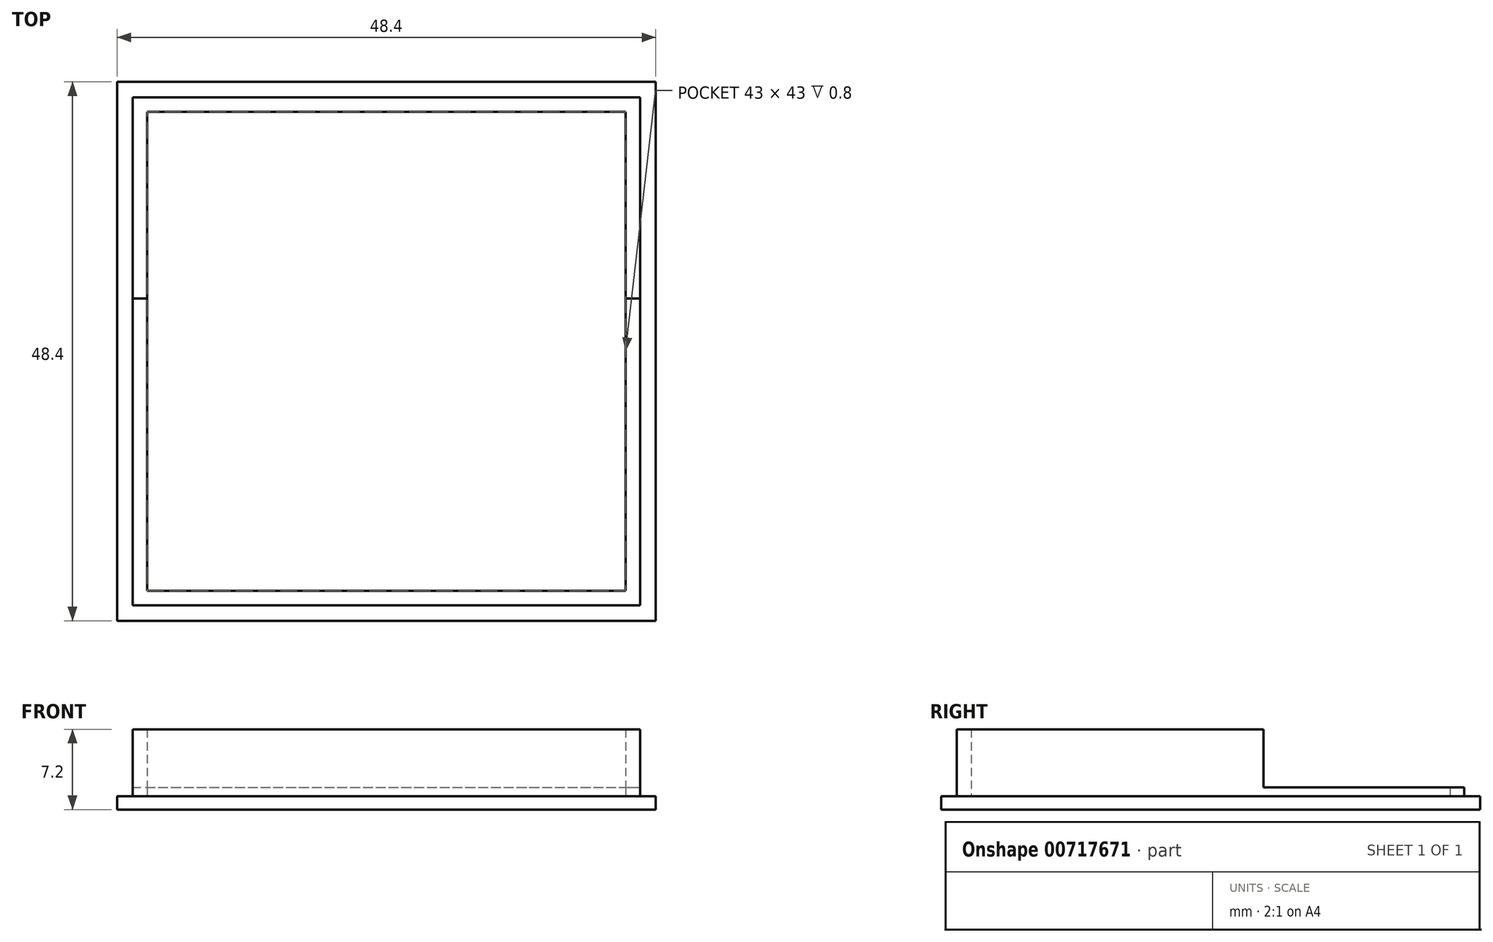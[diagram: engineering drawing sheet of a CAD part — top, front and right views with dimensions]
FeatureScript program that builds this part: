
annotation { "Feature Type Name" : "Feature", "Feature Type Description" : "" }
export const myFeature = defineFeature(function(context is Context, id is Id, definition is map)
    precondition{}
    {
        {
            var Q0;
            Q0=qCreatedBy(makeId("Top.planeOp"),FACE);
            var sketch = newSketch(context, id + "F0", { "sketchPlane" : qUnion([Q0])});
            skLineSegment(sketch, "E0.bottom", {"start": v(-24.2, 23.52) * mm, "end": v(24.2, 23.52) * mm});
            skLineSegment(sketch, "E0.top", {"start": v(-24.2, -24.88) * mm, "end": v(24.2, -24.88) * mm});
            skLineSegment(sketch, "E0.left", {"start": v(-24.2, 23.52) * mm, "end": v(-24.2, -24.88) * mm});
            skLineSegment(sketch, "E0.right", {"start": v(24.2, 23.52) * mm, "end": v(24.2, -24.88) * mm});
            skLineSegment(sketch, "E1.bottom", {"start": v(-22.8, 22.12) * mm, "end": v(22.8, 22.12) * mm});
            skLineSegment(sketch, "E1.top", {"start": v(-22.8, -23.48) * mm, "end": v(22.8, -23.48) * mm});
            skLineSegment(sketch, "E1.left", {"start": v(-22.8, 22.12) * mm, "end": v(-22.8, -23.48) * mm});
            skLineSegment(sketch, "E1.right", {"start": v(22.8, 22.12) * mm, "end": v(22.8, -23.48) * mm});
            skLineSegment(sketch, "E2.bottom", {"start": v(-21.5, 20.82) * mm, "end": v(21.5, 20.82) * mm});
            skLineSegment(sketch, "E2.top", {"start": v(-21.5, -22.18) * mm, "end": v(21.5, -22.18) * mm});
            skLineSegment(sketch, "E2.left", {"start": v(-21.5, 20.82) * mm, "end": v(-21.5, -22.18) * mm});
            skLineSegment(sketch, "E2.right", {"start": v(21.5, 20.82) * mm, "end": v(21.5, -22.18) * mm});
            skLineSegment(sketch, "E3", {"start": v(-22.8, 4.07) * mm, "end": v(-21.5, 4.07) * mm});
            skLineSegment(sketch, "E4", {"start": v(21.5, 4.07) * mm, "end": v(22.8, 4.07) * mm});
            skSolve(sketch);
        }
        {
            var Q0;
            Q0=qCreatedBy(makeId("Top.planeOp"),FACE);
            var sketch = newSketch(context, id + "F1", { "sketchPlane" : qUnion([Q0])});
            skLineSegment(sketch, "E5.bottom", {"start": v(-24.2, 23.52) * mm, "end": v(24.2, 23.52) * mm});
            skLineSegment(sketch, "E5.top", {"start": v(-24.2, -24.88) * mm, "end": v(24.2, -24.88) * mm});
            skLineSegment(sketch, "E5.left", {"start": v(-24.2, 23.52) * mm, "end": v(-24.2, -24.88) * mm});
            skLineSegment(sketch, "E5.right", {"start": v(24.2, 23.52) * mm, "end": v(24.2, -24.88) * mm});
            skLineSegment(sketch, "E6.bottom", {"start": v(-22.8, 22.12) * mm, "end": v(22.8, 22.12) * mm});
            skLineSegment(sketch, "E6.top", {"start": v(-22.8, -23.48) * mm, "end": v(22.8, -23.48) * mm});
            skLineSegment(sketch, "E6.left", {"start": v(-22.8, 22.12) * mm, "end": v(-22.8, -23.48) * mm});
            skLineSegment(sketch, "E6.right", {"start": v(22.8, 22.12) * mm, "end": v(22.8, -23.48) * mm});
            skLineSegment(sketch, "E7.bottom", {"start": v(-21.5, 20.82) * mm, "end": v(21.5, 20.82) * mm});
            skLineSegment(sketch, "E7.top", {"start": v(-21.5, -22.18) * mm, "end": v(21.5, -22.18) * mm});
            skLineSegment(sketch, "E7.left", {"start": v(-21.5, 20.82) * mm, "end": v(-21.5, -22.18) * mm});
            skLineSegment(sketch, "E7.right", {"start": v(21.5, 20.82) * mm, "end": v(21.5, -22.18) * mm});
            skLineSegment(sketch, "E8", {"start": v(-22.8, 4.07) * mm, "end": v(-21.5, 4.07) * mm});
            skLineSegment(sketch, "E9", {"start": v(21.5, 4.07) * mm, "end": v(22.8, 4.07) * mm});
            skSolve(sketch);
        }
        {
            var Q0;
            Q0=qCreatedBy(makeId("Top.planeOp"),FACE);
            var sketch = newSketch(context, id + "F2", { "sketchPlane" : qUnion([Q0])});
            skLineSegment(sketch, "E10.bottom", {"start": v(-24.2, 23.52) * mm, "end": v(24.2, 23.52) * mm});
            skLineSegment(sketch, "E10.top", {"start": v(-24.2, -24.88) * mm, "end": v(24.2, -24.88) * mm});
            skLineSegment(sketch, "E10.left", {"start": v(-24.2, 23.52) * mm, "end": v(-24.2, -24.88) * mm});
            skLineSegment(sketch, "E10.right", {"start": v(24.2, 23.52) * mm, "end": v(24.2, -24.88) * mm});
            skLineSegment(sketch, "E11.bottom", {"start": v(-22.8, 22.12) * mm, "end": v(22.8, 22.12) * mm});
            skLineSegment(sketch, "E11.top", {"start": v(-22.8, -23.48) * mm, "end": v(22.8, -23.48) * mm});
            skLineSegment(sketch, "E11.left", {"start": v(-22.8, 22.12) * mm, "end": v(-22.8, -23.48) * mm});
            skLineSegment(sketch, "E11.right", {"start": v(22.8, 22.12) * mm, "end": v(22.8, -23.48) * mm});
            skLineSegment(sketch, "E12.bottom", {"start": v(-21.5, 20.82) * mm, "end": v(21.5, 20.82) * mm});
            skLineSegment(sketch, "E12.top", {"start": v(-21.5, -22.18) * mm, "end": v(21.5, -22.18) * mm});
            skLineSegment(sketch, "E12.left", {"start": v(-21.5, 20.82) * mm, "end": v(-21.5, -22.18) * mm});
            skLineSegment(sketch, "E12.right", {"start": v(21.5, 20.82) * mm, "end": v(21.5, -22.18) * mm});
            skLineSegment(sketch, "E13", {"start": v(-22.8, 4.07) * mm, "end": v(-21.5, 4.07) * mm});
            skLineSegment(sketch, "E14", {"start": v(21.5, 4.07) * mm, "end": v(22.8, 4.07) * mm});
            skSolve(sketch);
        }
        {
            var Q0;
            Q0 = qSketchRegion(id + "F0", true);
            var Q1;
            {var subQ3=sQuery(id+"F0.wireOp",EDGE,"E2.bottom");Q1=makeQuery(id+"F0.imprint","IMPRINT",FACE,{"disambiguationData":[TD([[makeQuery(id+"F0.imprint","IMPRINT",EDGE,{"derivedFrom":subQ3}),-1.0]])]});}
            var Q2;
            {var subQ2=sQuery(id+"F0.wireOp",EDGE,"E1.bottom");Q2=makeQuery(id+"F0.imprint","IMPRINT",FACE,{"disambiguationData":[TD([[makeQuery(id+"F0.imprint","IMPRINT",EDGE,{"derivedFrom":subQ2}),-1.0]])]});}
            var Q3;
            {var subQ2=sQuery(id+"F0.wireOp",EDGE,"E1.top");Q3=makeQuery(id+"F0.imprint","IMPRINT",FACE,{"disambiguationData":[TD([[makeQuery(id+"F0.imprint","IMPRINT",EDGE,{"derivedFrom":subQ2}),1.0]])]});}
            extrude(context, id + "F3", {"entities" : qUnion([Q0, Q1, Q2, Q3]), "depth" : 1.2 * mm, "offsetDistance" : 25 * mm});
        }
        {
            var Q0;
            {var subQ2=sQuery(id+"F1.wireOp",EDGE,"E6.top");Q0=makeQuery(id+"F1.imprint","IMPRINT",FACE,{"disambiguationData":[TD([[makeQuery(id+"F1.imprint","IMPRINT",EDGE,{"derivedFrom":subQ2}),1.0]])]});}
            extrude(context, id + "F4", {"entities" : qUnion([Q0]), "operationType" : NewBodyOperationType.ADD, "depth" : 7.2 * mm, "offsetDistance" : 25 * mm});
        }
        {
            var Q0;
            {var subQ2=sQuery(id+"F2.wireOp",EDGE,"E11.bottom");Q0=makeQuery(id+"F2.imprint","IMPRINT",FACE,{"disambiguationData":[TD([[makeQuery(id+"F2.imprint","IMPRINT",EDGE,{"derivedFrom":subQ2}),-1.0]])]});}
            extrude(context, id + "F5", {"entities" : qUnion([Q0]), "operationType" : NewBodyOperationType.ADD, "depth" : 2 * mm, "offsetDistance" : 25 * mm});
        }
    });
